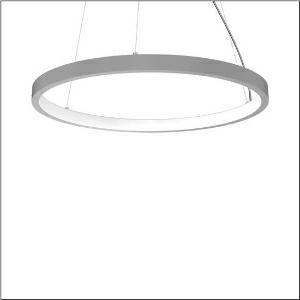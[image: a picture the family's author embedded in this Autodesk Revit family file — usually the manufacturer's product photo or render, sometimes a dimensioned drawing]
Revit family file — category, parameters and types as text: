
# Revit family: silica_21_ring-i_5pjbi4d3204a
name_source: partatom
category: Lighting Fixtures
units: mm (PartAtom-declared; Revit-internal decimal feet)

## family parameters
Cut with Voids When Loaded = No
Host = Face
Light Source = No
Part Type = Normal
Room Calculation Point = No
Round Connector Dimension = Use Diameter
Shared = No

## types (1)
- Silica 21 Ring-I (1 x LED, 8890 lm, 140 W, 4000K)
    Apparent Load = 140 VA
    CIE Flux Codes = 22 48 76 50 101
    Color Rendering = 80
    Color Temperature = 4000K
    Default Elevation = 1800 mm
    Description = Silica 21 Ring-I, suspended luminaire, of PMMA, frosted, light emission: inner ring side luminous distribution, primary light characteristic: symmetric, installation type: suspended mounting, LED, rated luminous flux: 8.890lm, luminous efficacy: 64lm/W, light colour: 840, colour temperature: 4000K, control gear: DALI 2, with terminal, 5-pole, mains connection: 230V, AC/DC, 0/50..60Hz, rated input power: 140W, housing, of extruded aluminium section, metallic grey (RAL 9006), diameter: 1.470mm, ceiling canopy, metallic grey (RAL 9006), protection rating (lamp compartment): IP40, insulation class (complete): insulation class I (protective earthing), certification: CE, impact resistance: IK02, permissible operating ambient temperature: 0..+35°C, packaging unit: 1 piece
    Height = 48 mm  [stored 0.15748 ft]
    Lamp = 1 x LED
    Lamp Light Flux = 8890 lm
    Lamp Power = 140 W
    Lamp count = 1
    Length = 1470 mm
    Luminous efficacy = 64 lm/W
    Manufacturer = Siteco
    ModVariant = No
    Model = 5PJBI4D3204A
    Mounting Place = Ceiling
    Mounting Type = Pendant
    Number of Poles = 1
    OnlyDefault = Yes
    Power Factor = 1
    Product Name = Silica 21 Ring-I
    Product group = suspended luminaire
    ProductGroupID = 904
    Protection Class = Protection class I
    Protection Degree = IP 40
    RLX_Detail_Level = 1
    RLX_Emergency_Light_Flux = 0 lm
    RLX_Emergency_Type = 0
    RLX_Emergency_Type_DB = No
    RlxData = <blob elided: 18829 chars, md5=f0406130>
    Socket = socket
    Standby Power = 0 W
    System Light Flux = 8890 lm
    System Power = 140 W
    Type Comments = Product without accessories
    Type Image = l_1251756.jpg
    URL = http://relux.com
    VarID = ---
    Voltage = 0 V
    Weight = 0.00 kg
    Width = 0 mm  [stored 0 ft]

note: [stored X ft] marks values corroborated as IEEE doubles in the binary element streams (Revit-internal decimal feet)

## geometry (parser evidence)
native form markers: Blend x4, Sweep x12
no freeform markers — native parametric forms only
